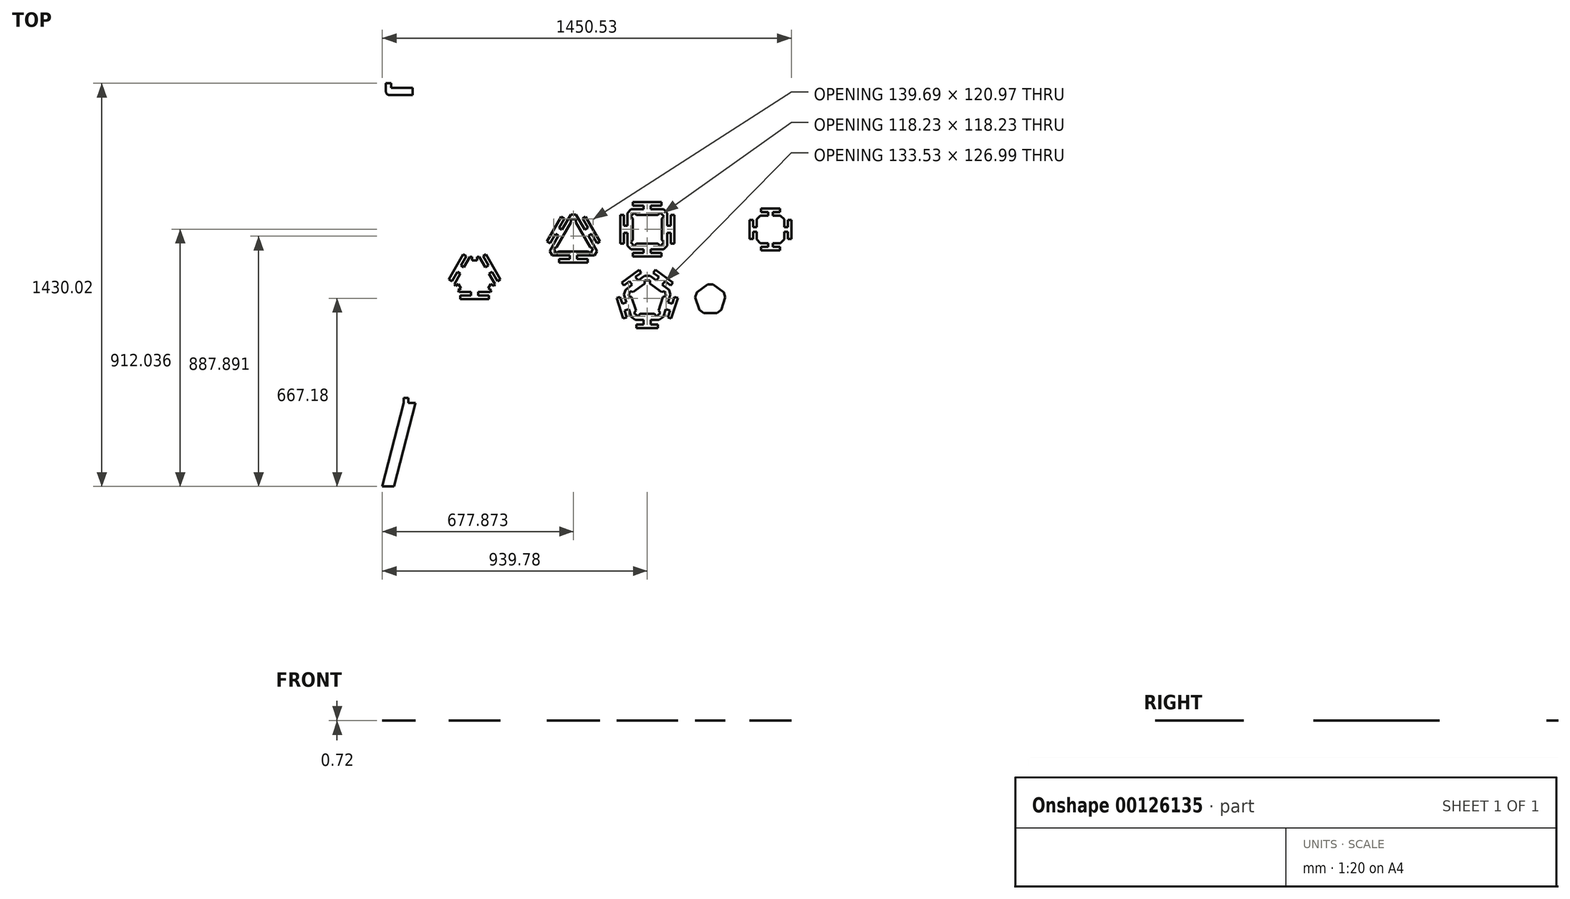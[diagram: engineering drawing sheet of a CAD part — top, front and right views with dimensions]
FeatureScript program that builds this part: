
annotation { "Feature Type Name" : "Feature", "Feature Type Description" : "" }
export const myFeature = defineFeature(function(context is Context, id is Id, definition is map)
    precondition{}
    {
        {
            assignVariable(context, id + "F0", {"name" : "ply34", "anyValue" : 0.72});
        }
        {
            var Q0;
            Q0=qCreatedBy(makeId("Top.planeOp"),FACE);
            var sketch = newSketch(context, id + "F1", { "sketchPlane" : qUnion([Q0])});
            skLineSegment(sketch, "E0.bottom", {"start": v(0, 0) * mm, "end": v(31.75, 0) * mm});
            skLineSegment(sketch, "E0.top", {"start": v(0, 711.2) * mm, "end": v(31.75, 711.2) * mm});
            skLineSegment(sketch, "E0.left", {"start": v(0, 0) * mm, "end": v(0, 711.2) * mm});
            skLineSegment(sketch, "E0.right", {"start": v(31.75, 0) * mm, "end": v(31.75, 711.2) * mm});
            skLineSegment(sketch, "E1.bottom", {"start": v(0, 0) * mm, "end": v(41.9, 0) * mm});
            skLineSegment(sketch, "E1.top", {"start": v(0, -406.4) * mm, "end": v(41.91, -406.4) * mm});
            skLineSegment(sketch, "E1.left", {"start": v(0, 0) * mm, "end": v(0, -406.4) * mm});
            skLineSegment(sketch, "E1.right", {"start": v(41.9, 0) * mm, "end": v(41.91, -406.4) * mm});
            skLineSegment(sketch, "E2.bottom", {"start": v(31.75, 711.2) * mm, "end": v(-44.45, 711.2) * mm});
            skLineSegment(sketch, "E2.top", {"start": v(31.75, 685.8) * mm, "end": v(-44.45, 685.8) * mm});
            skLineSegment(sketch, "E2.left", {"start": v(31.75, 711.2) * mm, "end": v(31.75, 685.8) * mm});
            skLineSegment(sketch, "E2.right", {"start": v(-44.45, 711.2) * mm, "end": v(-44.45, 685.8) * mm});
            skLineSegment(sketch, "E3.bottom", {"start": v(-44.45, 685.8) * mm, "end": v(-50.8, 685.8) * mm});
            skLineSegment(sketch, "E3.top", {"start": v(-44.45, 727.7) * mm, "end": v(-63.5, 727.7) * mm});
            skLineSegment(sketch, "E3.left", {"start": v(-44.45, 685.8) * mm, "end": v(-44.45, 727.7) * mm});
            skLineSegment(sketch, "E3.right", {"start": v(-63.5, 698.5) * mm, "end": v(-63.5, 727.7) * mm});
            skLineSegment(sketch, "E4.bottom", {"start": v(31.75, 711.2) * mm, "end": v(12.7, 711.2) * mm});
            skLineSegment(sketch, "E4.top", {"start": v(31.75, 727.7) * mm, "end": v(12.7, 727.7) * mm});
            skLineSegment(sketch, "E4.left", {"start": v(31.75, 711.2) * mm, "end": v(31.75, 727.7) * mm});
            skLineSegment(sketch, "E4.right", {"start": v(12.7, 711.2) * mm, "end": v(12.7, 727.7) * mm});
            skLineSegment(sketch, "E5.bottom", {"start": v(0, -406.4) * mm, "end": v(16.51, -406.4) * mm});
            skLineSegment(sketch, "E5.top", {"start": v(0, -388.11) * mm, "end": v(16.51, -388.11) * mm});
            skLineSegment(sketch, "E5.left", {"start": v(0, -406.4) * mm, "end": v(0, -388.11) * mm});
            skLineSegment(sketch, "E5.right", {"start": v(16.51, -406.4) * mm, "end": v(16.51, -388.11) * mm});
            skLineSegment(sketch, "E6.bottom", {"start": v(0, 431.8) * mm, "end": v(16.51, 431.8) * mm});
            skLineSegment(sketch, "E6.top", {"start": v(0, 413.51) * mm, "end": v(16.51, 413.51) * mm});
            skLineSegment(sketch, "E6.left", {"start": v(0, 431.8) * mm, "end": v(0, 413.51) * mm});
            skLineSegment(sketch, "E6.right", {"start": v(16.51, 431.8) * mm, "end": v(16.51, 413.51) * mm});
            skLineSegment(sketch, "E7.0", {"start": v(194.06, 15.84) * mm, "end": v(242.06, 98.99) * mm});
            skLineSegment(sketch, "E7.1", {"start": v(260.35, 98.99) * mm, "end": v(308.36, 15.84) * mm});
            skLineSegment(sketch, "E7.2", {"start": v(299.21, 0) * mm, "end": v(203.2, 0) * mm});
            skLineSegment(sketch, "E8", {"start": v(242.06, 98.99) * mm, "end": v(260.35, 98.99) * mm});
            skLineSegment(sketch, "E9", {"start": v(308.36, 15.84) * mm, "end": v(299.21, 0) * mm});
            skLineSegment(sketch, "E10", {"start": v(194.06, 15.84) * mm, "end": v(203.2, 0) * mm});
            skLineSegment(sketch, "E11.0", {"start": v(541.73, 146.65) * mm, "end": v(592.53, 234.64) * mm});
            skLineSegment(sketch, "E11.1", {"start": v(610.82, 234.64) * mm, "end": v(661.62, 146.65) * mm});
            skLineSegment(sketch, "E11.2", {"start": v(652.47, 130.81) * mm, "end": v(550.87, 130.81) * mm});
            skLineSegment(sketch, "E12", {"start": v(592.53, 234.64) * mm, "end": v(610.82, 234.64) * mm});
            skLineSegment(sketch, "E13", {"start": v(661.62, 146.65) * mm, "end": v(652.47, 130.81) * mm});
            skLineSegment(sketch, "E14", {"start": v(541.73, 146.65) * mm, "end": v(550.87, 130.81) * mm});
            skLineSegment(sketch, "E15.0", {"start": v(517.53, 132.68) * mm, "end": v(592.53, 262.58) * mm});
            skLineSegment(sketch, "E15.1", {"start": v(610.82, 262.58) * mm, "end": v(685.81, 132.68) * mm});
            skLineSegment(sketch, "E15.2", {"start": v(685.81, 132.68) * mm, "end": v(676.67, 116.84) * mm});
            skLineSegment(sketch, "E15.3", {"start": v(592.53, 262.58) * mm, "end": v(610.82, 262.58) * mm});
            skLineSegment(sketch, "E15.4", {"start": v(676.67, 116.84) * mm, "end": v(526.68, 116.84) * mm});
            skLineSegment(sketch, "E15.5", {"start": v(517.53, 132.68) * mm, "end": v(526.68, 116.84) * mm});
            skPoint(sketch, "E16", {"position": v(657.04, 138.73) * mm});
            skPoint(sketch, "E17", {"position": v(546.3, 138.73) * mm});
            skLineSegment(sketch, "E18", {"start": v(601.67, 234.64) * mm, "end": v(601.67, 130.81) * mm, "construction": true});
            skLineSegment(sketch, "E19", {"start": v(657.04, 138.73) * mm, "end": v(506.57, 225.6) * mm, "construction": true});
            skLineSegment(sketch, "E20", {"start": v(546.3, 138.73) * mm, "end": v(636.22, 190.64) * mm, "construction": true});
            skPoint(sketch, "E21", {"position": v(601.67, 272.41) * mm});
            skLineSegment(sketch, "E22.top", {"start": v(592.53, 246.07) * mm, "end": v(610.82, 246.07) * mm});
            skLineSegment(sketch, "E22.left", {"start": v(592.53, 234.64) * mm, "end": v(592.53, 246.07) * mm});
            skLineSegment(sketch, "E22.right", {"start": v(610.82, 234.64) * mm, "end": v(610.82, 246.07) * mm});
            skPoint(sketch, "E23", {"position": v(601.67, 170.7) * mm});
            skLineSegment(sketch, "E24.1.0", {"start": v(540.97, 125.1) * mm, "end": v(531.83, 140.93) * mm});
            skLineSegment(sketch, "E24.1.1", {"start": v(550.87, 130.8) * mm, "end": v(540.97, 125.1) * mm});
            skLineSegment(sketch, "E24.1.2", {"start": v(541.73, 146.65) * mm, "end": v(531.83, 140.93) * mm});
            skLineSegment(sketch, "E24.2.0", {"start": v(671.52, 140.93) * mm, "end": v(662.37, 125.1) * mm});
            skLineSegment(sketch, "E24.2.1", {"start": v(661.62, 146.65) * mm, "end": v(671.52, 140.93) * mm});
            skLineSegment(sketch, "E24.2.2", {"start": v(652.47, 130.81) * mm, "end": v(662.37, 125.1) * mm});
            skLineSegment(sketch, "E25.0", {"start": v(-364.74, -24.05) * mm, "end": v(-313.94, 63.94) * mm, "construction": true});
            skLineSegment(sketch, "E25.1", {"start": v(-295.66, 63.94) * mm, "end": v(-244.86, -24.05) * mm, "construction": true});
            skLineSegment(sketch, "E25.2", {"start": v(-254, -39.89) * mm, "end": v(-355.6, -39.89) * mm, "construction": true});
            skLineSegment(sketch, "E26", {"start": v(-313.94, 63.94) * mm, "end": v(-295.66, 63.94) * mm, "construction": true});
            skLineSegment(sketch, "E27.0", {"start": v(-398.47, -24.05) * mm, "end": v(-330.8, 93.15) * mm, "construction": true});
            skLineSegment(sketch, "E27.1", {"start": v(-278.8, 93.15) * mm, "end": v(-211.13, -24.05) * mm, "construction": true});
            skLineSegment(sketch, "E27.2", {"start": v(-211.13, -24.05) * mm, "end": v(-237.14, -69.1) * mm, "construction": true});
            skLineSegment(sketch, "E27.3", {"start": v(-330.8, 93.15) * mm, "end": v(-278.8, 93.15) * mm, "construction": true});
            skLineSegment(sketch, "E27.4", {"start": v(-237.14, -69.1) * mm, "end": v(-372.46, -69.1) * mm, "construction": true});
            skLineSegment(sketch, "E28", {"start": v(-304.8, 63.94) * mm, "end": v(-304.8, -39.89) * mm, "construction": true});
            skLineSegment(sketch, "E29", {"start": v(-360.17, -31.97) * mm, "end": v(-270.26, 19.94) * mm, "construction": true});
            skPoint(sketch, "E30", {"position": v(-304.8, 109) * mm});
            skLineSegment(sketch, "E31.top", {"start": v(-313.94, 76.64) * mm, "end": v(-295.66, 76.64) * mm, "construction": true});
            skLineSegment(sketch, "E31.left", {"start": v(-313.94, 63.94) * mm, "end": v(-313.94, 76.64) * mm, "construction": true});
            skLineSegment(sketch, "E31.right", {"start": v(-295.66, 63.94) * mm, "end": v(-295.66, 76.64) * mm, "construction": true});
            skLineSegment(sketch, "E32.bottom", {"start": v(-313.94, 89.34) * mm, "end": v(-295.66, 89.34) * mm});
            skLineSegment(sketch, "E32.top", {"start": v(-313.94, 51.24) * mm, "end": v(-295.66, 51.24) * mm});
            skLineSegment(sketch, "E32.left", {"start": v(-313.94, 89.34) * mm, "end": v(-313.94, 51.24) * mm});
            skLineSegment(sketch, "E32.right", {"start": v(-295.66, 89.34) * mm, "end": v(-295.66, 51.24) * mm});
            skLineSegment(sketch, "E33.top", {"start": v(-313.94, 38.54) * mm, "end": v(-295.66, 38.54) * mm});
            skLineSegment(sketch, "E33.left", {"start": v(-313.94, 89.34) * mm, "end": v(-313.94, 38.54) * mm});
            skLineSegment(sketch, "E33.right", {"start": v(-295.66, 89.34) * mm, "end": v(-295.66, 38.54) * mm});
            skLineSegment(sketch, "E34.bottom", {"start": v(-295.66, 89.34) * mm, "end": v(-313.94, 89.34) * mm});
            skLineSegment(sketch, "E34.top", {"start": v(-295.66, 76.64) * mm, "end": v(-313.94, 76.64) * mm});
            skLineSegment(sketch, "E34.left", {"start": v(-295.66, 89.34) * mm, "end": v(-295.66, 76.64) * mm});
            skLineSegment(sketch, "E34.right", {"start": v(-313.94, 89.34) * mm, "end": v(-313.94, 76.64) * mm});
            skLineSegment(sketch, "E35.0", {"start": v(179.4, 15.84) * mm, "end": v(195.87, -12.7) * mm});
            skLineSegment(sketch, "E35.1", {"start": v(234.73, 111.69) * mm, "end": v(267.68, 111.69) * mm});
            skLineSegment(sketch, "E35.2", {"start": v(267.68, 111.69) * mm, "end": v(323.02, 15.84) * mm});
            skLineSegment(sketch, "E35.3", {"start": v(179.4, 15.84) * mm, "end": v(234.73, 111.69) * mm});
            skLineSegment(sketch, "E35.4", {"start": v(323.02, 15.84) * mm, "end": v(306.54, -12.7) * mm});
            skLineSegment(sketch, "E35.5", {"start": v(306.54, -12.7) * mm, "end": v(195.87, -12.7) * mm});
            skLineSegment(sketch, "E36", {"start": v(242.06, 98.99) * mm, "end": v(242.06, 111.69) * mm});
            skLineSegment(sketch, "E37", {"start": v(260.35, 98.99) * mm, "end": v(260.35, 111.69) * mm});
            skLineSegment(sketch, "E38", {"start": v(251.2, 98.99) * mm, "end": v(251.2, 0) * mm, "construction": true});
            skLineSegment(sketch, "E39", {"start": v(303.78, 7.92) * mm, "end": v(218.06, 57.41) * mm, "construction": true});
            skPoint(sketch, "E39.endSnap0", {"position": v(218.06, 57.41) * mm});
            skPoint(sketch, "E40", {"position": v(251.2, 38.27) * mm});
            skLineSegment(sketch, "E41.1.0", {"start": v(194.06, 15.84) * mm, "end": v(183.06, 9.49) * mm});
            skLineSegment(sketch, "E41.1.1", {"start": v(203.2, 0) * mm, "end": v(192.2, -6.35) * mm});
            skLineSegment(sketch, "E41.1.2", {"start": v(203.2, 0) * mm, "end": v(194.06, 15.84) * mm});
            skLineSegment(sketch, "E41.2.0", {"start": v(299.21, 0) * mm, "end": v(310.21, -6.35) * mm});
            skLineSegment(sketch, "E41.2.1", {"start": v(308.36, 15.84) * mm, "end": v(319.35, 9.49) * mm});
            skLineSegment(sketch, "E42", {"start": v(-364.74, -24.05) * mm, "end": v(-355.6, -39.89) * mm, "construction": true});
            skLineSegment(sketch, "E43", {"start": v(-254, -39.89) * mm, "end": v(-244.86, -24.05) * mm, "construction": true});
            skLineSegment(sketch, "E44", {"start": v(-398.47, -24.05) * mm, "end": v(-372.46, -69.1) * mm, "construction": true});
            skPoint(sketch, "E45", {"position": v(-304.8, 0) * mm});
            skLineSegment(sketch, "E46.1.0", {"start": v(-333.6, -27.19) * mm, "end": v(-342.75, -11.35) * mm});
            skLineSegment(sketch, "E46.1.1", {"start": v(-355.6, -39.89) * mm, "end": v(-364.74, -24.05) * mm, "construction": true});
            skLineSegment(sketch, "E46.1.2", {"start": v(-377.6, -52.59) * mm, "end": v(-386.74, -36.75) * mm});
            skLineSegment(sketch, "E46.1.3", {"start": v(-377.6, -52.59) * mm, "end": v(-366.6, -46.24) * mm});
            skLineSegment(sketch, "E46.1.4", {"start": v(-386.74, -36.75) * mm, "end": v(-353.75, -17.7) * mm});
            skLineSegment(sketch, "E46.1.5", {"start": v(-344.6, -33.54) * mm, "end": v(-353.75, -17.7) * mm});
            skLineSegment(sketch, "E46.1.6", {"start": v(-366.6, -46.24) * mm, "end": v(-375.74, -30.4) * mm, "construction": true});
            skLineSegment(sketch, "E46.1.7", {"start": v(-377.6, -52.59) * mm, "end": v(-344.6, -33.54) * mm});
            skLineSegment(sketch, "E46.1.8", {"start": v(-377.6, -52.59) * mm, "end": v(-333.6, -27.19) * mm});
            skLineSegment(sketch, "E46.1.9", {"start": v(-364.74, -24.05) * mm, "end": v(-375.74, -30.4) * mm, "construction": true});
            skLineSegment(sketch, "E46.1.10", {"start": v(-386.74, -36.75) * mm, "end": v(-342.75, -11.35) * mm});
            skLineSegment(sketch, "E46.1.11", {"start": v(-355.6, -39.89) * mm, "end": v(-366.6, -46.24) * mm, "construction": true});
            skPoint(sketch, "E46.1.12", {"position": v(-399.2, -54.5) * mm});
            skLineSegment(sketch, "E46.1.13", {"start": v(-375.74, -30.4) * mm, "end": v(-366.6, -46.24) * mm});
            skLineSegment(sketch, "E46.1.14", {"start": v(-386.74, -36.75) * mm, "end": v(-375.74, -30.4) * mm});
            skLineSegment(sketch, "E46.1.15", {"start": v(-386.74, -36.75) * mm, "end": v(-377.6, -52.59) * mm});
            skLineSegment(sketch, "E46.1.16", {"start": v(-355.6, -39.89) * mm, "end": v(-364.74, -24.05) * mm, "construction": true});
            skLineSegment(sketch, "E46.1.17", {"start": v(-377.6, -52.59) * mm, "end": v(-386.74, -36.75) * mm});
            skLineSegment(sketch, "E46.2.0", {"start": v(-266.85, -11.35) * mm, "end": v(-276, -27.19) * mm});
            skLineSegment(sketch, "E46.2.1", {"start": v(-244.86, -24.05) * mm, "end": v(-254, -39.89) * mm, "construction": true});
            skLineSegment(sketch, "E46.2.2", {"start": v(-222.86, -36.75) * mm, "end": v(-232, -52.59) * mm});
            skLineSegment(sketch, "E46.2.3", {"start": v(-222.86, -36.75) * mm, "end": v(-233.86, -30.4) * mm});
            skLineSegment(sketch, "E46.2.4", {"start": v(-232, -52.59) * mm, "end": v(-265, -33.54) * mm});
            skLineSegment(sketch, "E46.2.5", {"start": v(-255.85, -17.7) * mm, "end": v(-265, -33.54) * mm});
            skLineSegment(sketch, "E46.2.6", {"start": v(-233.86, -30.4) * mm, "end": v(-243, -46.24) * mm, "construction": true});
            skLineSegment(sketch, "E46.2.7", {"start": v(-222.86, -36.75) * mm, "end": v(-255.85, -17.7) * mm});
            skLineSegment(sketch, "E46.2.8", {"start": v(-222.86, -36.75) * mm, "end": v(-266.85, -11.35) * mm});
            skLineSegment(sketch, "E46.2.9", {"start": v(-254, -39.89) * mm, "end": v(-243, -46.24) * mm, "construction": true});
            skLineSegment(sketch, "E46.2.10", {"start": v(-232, -52.59) * mm, "end": v(-276, -27.19) * mm});
            skLineSegment(sketch, "E46.2.11", {"start": v(-244.86, -24.05) * mm, "end": v(-233.86, -30.4) * mm, "construction": true});
            skPoint(sketch, "E46.2.12", {"position": v(-210.4, -54.5) * mm});
            skLineSegment(sketch, "E46.2.13", {"start": v(-243, -46.24) * mm, "end": v(-233.86, -30.4) * mm});
            skLineSegment(sketch, "E46.2.14", {"start": v(-232, -52.59) * mm, "end": v(-243, -46.24) * mm});
            skLineSegment(sketch, "E46.2.15", {"start": v(-232, -52.59) * mm, "end": v(-222.86, -36.75) * mm});
            skLineSegment(sketch, "E46.2.16", {"start": v(-244.86, -24.05) * mm, "end": v(-254, -39.89) * mm, "construction": true});
            skLineSegment(sketch, "E46.2.17", {"start": v(-222.86, -36.75) * mm, "end": v(-232, -52.59) * mm});
            skPoint(sketch, "E47", {"position": v(601.67, 116.84) * mm});
            skPoint(sketch, "E48", {"position": v(601.67, 262.58) * mm});
            skPoint(sketch, "E49", {"position": v(601.67, 246.07) * mm});
            skLineSegment(sketch, "E50", {"start": v(41.91, -406.4) * mm, "end": v(41.91, -702.31) * mm, "construction": true});
            skLineSegment(sketch, "E51", {"start": v(0, -406.4) * mm, "end": v(0, -702.31) * mm, "construction": true});
            skLineSegment(sketch, "E52", {"start": v(41.91, -457.2) * mm, "end": v(0, -457.2) * mm, "construction": true});
            skArc(sketch, "E53", {"start": v(-34.29, -702.31) * mm, "mid": v(26.28, -560.14) * mm, "end": v(41.91, -406.4) * mm, "construction": true});
            skArc(sketch, "E54", {"start": v(-76.2, -702.31) * mm, "mid": v(-15.63, -560.14) * mm, "end": v(0, -406.4) * mm, "construction": true});
            skLineSegment(sketch, "E55", {"start": v(-76.2, -702.31) * mm, "end": v(-34.29, -702.31) * mm});
            skPoint(sketch, "E56.visualSharp", {"position": v(-63.5, 685.8) * mm});
            skArc(sketch, "E56.filletArc", {"start": v(-63.5, 698.5) * mm, "mid": v(-59.78, 689.52) * mm, "end": v(-50.8, 685.8) * mm});
            skLineSegment(sketch, "E57.0", {"start": v(191.26, 297.58) * mm, "end": v(242.06, 385.57) * mm, "construction": true});
            skLineSegment(sketch, "E57.1", {"start": v(260.35, 385.57) * mm, "end": v(311.15, 297.58) * mm, "construction": true});
            skLineSegment(sketch, "E57.2", {"start": v(302, 281.75) * mm, "end": v(200.4, 281.75) * mm, "construction": true});
            skLineSegment(sketch, "E58", {"start": v(242.06, 385.57) * mm, "end": v(260.35, 385.57) * mm, "construction": true});
            skLineSegment(sketch, "E59", {"start": v(311.15, 297.58) * mm, "end": v(302, 281.75) * mm, "construction": true});
            skLineSegment(sketch, "E60", {"start": v(191.26, 297.58) * mm, "end": v(200.4, 281.75) * mm, "construction": true});
            skLineSegment(sketch, "E61.0", {"start": v(167.07, 283.61) * mm, "end": v(242.06, 413.51) * mm, "construction": true});
            skLineSegment(sketch, "E61.1", {"start": v(260.35, 413.51) * mm, "end": v(335.35, 283.61) * mm, "construction": true});
            skLineSegment(sketch, "E61.2", {"start": v(335.35, 283.61) * mm, "end": v(326.2, 267.78) * mm, "construction": true});
            skLineSegment(sketch, "E61.3", {"start": v(242.06, 413.51) * mm, "end": v(260.35, 413.51) * mm, "construction": true});
            skLineSegment(sketch, "E61.4", {"start": v(326.2, 267.78) * mm, "end": v(176.2, 267.78) * mm, "construction": true});
            skLineSegment(sketch, "E61.5", {"start": v(167.07, 283.61) * mm, "end": v(176.2, 267.78) * mm, "construction": true});
            skPoint(sketch, "E62", {"position": v(306.58, 289.66) * mm});
            skPoint(sketch, "E63", {"position": v(195.83, 289.66) * mm});
            skLineSegment(sketch, "E64", {"start": v(251.2, 385.57) * mm, "end": v(251.2, 281.75) * mm, "construction": true});
            skLineSegment(sketch, "E65", {"start": v(306.58, 289.66) * mm, "end": v(162.6, 372.8) * mm, "construction": true});
            skLineSegment(sketch, "E66", {"start": v(195.83, 289.66) * mm, "end": v(285.75, 341.58) * mm, "construction": true});
            skPoint(sketch, "E67", {"position": v(251.2, 431.16) * mm});
            skLineSegment(sketch, "E68.top", {"start": v(242.06, 397) * mm, "end": v(260.35, 397) * mm, "construction": true});
            skLineSegment(sketch, "E68.left", {"start": v(242.06, 385.57) * mm, "end": v(242.06, 397) * mm, "construction": true});
            skLineSegment(sketch, "E68.right", {"start": v(260.35, 385.57) * mm, "end": v(260.35, 397) * mm, "construction": true});
            skPoint(sketch, "E69", {"position": v(251.2, 321.63) * mm});
            skLineSegment(sketch, "E70.1.0", {"start": v(190.5, 276.03) * mm, "end": v(181.36, 291.87) * mm, "construction": true});
            skLineSegment(sketch, "E70.1.1", {"start": v(200.4, 281.75) * mm, "end": v(190.5, 276.03) * mm, "construction": true});
            skLineSegment(sketch, "E70.1.2", {"start": v(191.26, 297.58) * mm, "end": v(181.36, 291.87) * mm, "construction": true});
            skLineSegment(sketch, "E70.2.0", {"start": v(321.05, 291.87) * mm, "end": v(311.9, 276.03) * mm, "construction": true});
            skLineSegment(sketch, "E70.2.1", {"start": v(311.15, 297.58) * mm, "end": v(321.05, 291.87) * mm, "construction": true});
            skLineSegment(sketch, "E70.2.2", {"start": v(302, 281.75) * mm, "end": v(311.9, 276.03) * mm, "construction": true});
            skPoint(sketch, "E71", {"position": v(251.2, 267.78) * mm});
            skPoint(sketch, "E72", {"position": v(251.2, 413.51) * mm});
            skPoint(sketch, "E73", {"position": v(251.2, 397) * mm});
            skPoint(sketch, "E74", {"position": v(251.2, 111.69) * mm});
            skLineSegment(sketch, "E75.0", {"start": v(242.06, 381.76) * mm, "end": v(260.35, 381.76) * mm});
            skLineSegment(sketch, "E76.0", {"start": v(307.85, 299.49) * mm, "end": v(298.7, 283.65) * mm});
            skLineSegment(sketch, "E77.0", {"start": v(203.7, 283.65) * mm, "end": v(194.56, 299.49) * mm});
            skLineSegment(sketch, "E78", {"start": v(648.32, 197.63) * mm, "end": v(670.31, 210.33) * mm, "construction": true});
            skLineSegment(sketch, "E79", {"start": v(670.31, 210.33) * mm, "end": v(663.96, 221.33) * mm});
            skLineSegment(sketch, "E80", {"start": v(663.96, 221.33) * mm, "end": v(641.97, 208.63) * mm});
            skLineSegment(sketch, "E81.MirrorCS", {"start": v(670.31, 210.33) * mm, "end": v(676.66, 199.33) * mm});
            skLineSegment(sketch, "E82.MirrorCS", {"start": v(676.66, 199.33) * mm, "end": v(654.67, 186.63) * mm});
            skLineSegment(sketch, "E83", {"start": v(663.96, 221.33) * mm, "end": v(644.91, 254.32) * mm});
            skLineSegment(sketch, "E84.MirrorCS", {"start": v(676.66, 199.33) * mm, "end": v(695.71, 166.33) * mm});
            skLineSegment(sketch, "E85", {"start": v(644.91, 254.32) * mm, "end": v(633.91, 247.97) * mm});
            skLineSegment(sketch, "E86", {"start": v(633.91, 247.97) * mm, "end": v(652.96, 214.98) * mm});
            skLineSegment(sketch, "E87.MirrorCS", {"start": v(684.71, 159.98) * mm, "end": v(665.66, 192.98) * mm});
            skLineSegment(sketch, "E88.MirrorCS", {"start": v(695.71, 166.33) * mm, "end": v(684.71, 159.98) * mm});
            skLineSegment(sketch, "E89.1.0", {"start": v(518.63, 159.98) * mm, "end": v(537.68, 192.98) * mm});
            skLineSegment(sketch, "E89.1.1", {"start": v(507.63, 166.33) * mm, "end": v(518.63, 159.98) * mm});
            skLineSegment(sketch, "E89.1.2", {"start": v(526.68, 199.33) * mm, "end": v(507.63, 166.33) * mm});
            skLineSegment(sketch, "E89.1.3", {"start": v(533.03, 210.33) * mm, "end": v(526.68, 199.33) * mm});
            skLineSegment(sketch, "E89.1.4", {"start": v(533.03, 210.33) * mm, "end": v(539.38, 221.33) * mm});
            skLineSegment(sketch, "E89.1.5", {"start": v(526.68, 199.33) * mm, "end": v(548.68, 186.63) * mm});
            skLineSegment(sketch, "E89.1.6", {"start": v(539.38, 221.33) * mm, "end": v(561.38, 208.63) * mm});
            skLineSegment(sketch, "E89.1.7", {"start": v(569.43, 247.97) * mm, "end": v(550.38, 214.98) * mm});
            skLineSegment(sketch, "E89.1.8", {"start": v(539.38, 221.33) * mm, "end": v(558.43, 254.32) * mm});
            skLineSegment(sketch, "E89.1.9", {"start": v(558.43, 254.32) * mm, "end": v(569.43, 247.97) * mm});
            skLineSegment(sketch, "E89.2.0", {"start": v(652.47, 104.14) * mm, "end": v(614.37, 104.14) * mm});
            skLineSegment(sketch, "E89.2.1", {"start": v(652.47, 91.44) * mm, "end": v(652.47, 104.14) * mm});
            skLineSegment(sketch, "E89.2.2", {"start": v(614.37, 91.44) * mm, "end": v(652.47, 91.44) * mm});
            skLineSegment(sketch, "E89.2.3", {"start": v(601.67, 91.44) * mm, "end": v(614.37, 91.44) * mm});
            skLineSegment(sketch, "E89.2.4", {"start": v(601.67, 91.44) * mm, "end": v(588.97, 91.44) * mm});
            skLineSegment(sketch, "E89.2.5", {"start": v(614.37, 91.44) * mm, "end": v(614.37, 116.84) * mm});
            skLineSegment(sketch, "E89.2.6", {"start": v(588.97, 91.44) * mm, "end": v(588.97, 116.84) * mm});
            skLineSegment(sketch, "E89.2.7", {"start": v(550.87, 104.14) * mm, "end": v(588.97, 104.14) * mm});
            skLineSegment(sketch, "E89.2.8", {"start": v(588.97, 91.44) * mm, "end": v(550.87, 91.44) * mm});
            skLineSegment(sketch, "E89.2.9", {"start": v(550.87, 91.44) * mm, "end": v(550.87, 104.14) * mm});
            skLineSegment(sketch, "E90", {"start": v(295.35, 63.76) * mm, "end": v(317.35, 76.46) * mm, "construction": true});
            skLineSegment(sketch, "E91", {"start": v(317.35, 76.46) * mm, "end": v(291.95, 120.46) * mm});
            skLineSegment(sketch, "E92", {"start": v(291.95, 120.46) * mm, "end": v(280.95, 114.1) * mm});
            skLineSegment(sketch, "E93", {"start": v(280.95, 114.1) * mm, "end": v(300, 81.11) * mm});
            skLineSegment(sketch, "E94", {"start": v(300, 81.11) * mm, "end": v(289, 74.76) * mm});
            skLineSegment(sketch, "E95.MirrorCS", {"start": v(317.35, 76.46) * mm, "end": v(342.75, 32.47) * mm});
            skLineSegment(sketch, "E96.MirrorCS", {"start": v(342.75, 32.47) * mm, "end": v(331.75, 26.12) * mm});
            skLineSegment(sketch, "E97.MirrorCS", {"start": v(331.75, 26.12) * mm, "end": v(312.7, 59.11) * mm});
            skLineSegment(sketch, "E98.MirrorCS", {"start": v(312.7, 59.11) * mm, "end": v(301.7, 52.76) * mm});
            skLineSegment(sketch, "E99.1.0", {"start": v(189.71, 59.11) * mm, "end": v(200.71, 52.76) * mm});
            skLineSegment(sketch, "E99.1.1", {"start": v(202.41, 81.11) * mm, "end": v(213.41, 74.76) * mm});
            skLineSegment(sketch, "E99.1.2", {"start": v(170.66, 26.12) * mm, "end": v(189.71, 59.11) * mm});
            skLineSegment(sketch, "E99.1.3", {"start": v(185.06, 76.46) * mm, "end": v(159.66, 32.47) * mm});
            skLineSegment(sketch, "E99.1.4", {"start": v(207.06, 63.76) * mm, "end": v(185.06, 76.46) * mm, "construction": true});
            skLineSegment(sketch, "E99.1.5", {"start": v(159.66, 32.47) * mm, "end": v(170.66, 26.12) * mm});
            skLineSegment(sketch, "E99.1.6", {"start": v(185.06, 76.46) * mm, "end": v(210.46, 120.46) * mm});
            skLineSegment(sketch, "E99.1.7", {"start": v(210.46, 120.46) * mm, "end": v(221.46, 114.1) * mm});
            skLineSegment(sketch, "E99.1.8", {"start": v(221.46, 114.1) * mm, "end": v(202.41, 81.11) * mm});
            skLineSegment(sketch, "E99.2.0", {"start": v(263.9, -25.4) * mm, "end": v(263.9, -12.7) * mm});
            skLineSegment(sketch, "E99.2.1", {"start": v(238.5, -25.4) * mm, "end": v(238.5, -12.7) * mm});
            skLineSegment(sketch, "E99.2.2", {"start": v(302, -25.4) * mm, "end": v(263.9, -25.4) * mm});
            skLineSegment(sketch, "E99.2.3", {"start": v(251.2, -38.1) * mm, "end": v(302, -38.1) * mm});
            skLineSegment(sketch, "E99.2.4", {"start": v(251.2, -12.7) * mm, "end": v(251.2, -38.1) * mm, "construction": true});
            skLineSegment(sketch, "E99.2.5", {"start": v(302, -38.1) * mm, "end": v(302, -25.4) * mm});
            skLineSegment(sketch, "E99.2.6", {"start": v(251.2, -38.1) * mm, "end": v(200.4, -38.1) * mm});
            skLineSegment(sketch, "E99.2.7", {"start": v(200.4, -38.1) * mm, "end": v(200.4, -25.4) * mm});
            skLineSegment(sketch, "E99.2.8", {"start": v(200.4, -25.4) * mm, "end": v(238.5, -25.4) * mm});
            skLineSegment(sketch, "E100", {"start": v(0, -406.4) * mm, "end": v(-76.2, -702.31) * mm});
            skLineSegment(sketch, "E101", {"start": v(-34.29, -702.31) * mm, "end": v(41.91, -406.4) * mm});
            skLineSegment(sketch, "E102.bottom", {"start": v(792.8, 280.51) * mm, "end": v(934.37, 280.51) * mm});
            skLineSegment(sketch, "E102.top", {"start": v(792.8, 138.94) * mm, "end": v(934.37, 138.94) * mm});
            skLineSegment(sketch, "E102.left", {"start": v(792.8, 280.51) * mm, "end": v(792.8, 138.94) * mm});
            skLineSegment(sketch, "E102.right", {"start": v(934.37, 280.51) * mm, "end": v(934.37, 138.94) * mm});
            skLineSegment(sketch, "E103", {"start": v(805.72, 280.51) * mm, "end": v(792.8, 267.58) * mm});
            skLineSegment(sketch, "E104", {"start": v(805.72, 280.51) * mm, "end": v(825.48, 260.76) * mm, "construction": true});
            skLineSegment(sketch, "E105", {"start": v(825.48, 260.76) * mm, "end": v(812.55, 247.83) * mm});
            skLineSegment(sketch, "E106", {"start": v(812.55, 247.83) * mm, "end": v(792.8, 267.58) * mm, "construction": true});
            skLineSegment(sketch, "E107", {"start": v(812.55, 247.83) * mm, "end": v(804.47, 255.9) * mm});
            skLineSegment(sketch, "E108", {"start": v(804.47, 255.9) * mm, "end": v(817.4, 268.84) * mm});
            skLineSegment(sketch, "E109", {"start": v(817.4, 268.84) * mm, "end": v(825.48, 260.76) * mm});
            skPoint(sketch, "E110", {"position": v(863.58, 209.73) * mm});
            skPoint(sketch, "E110.positionSnap0", {"position": v(792.8, 209.73) * mm});
            skPoint(sketch, "E110.positionSnap1", {"position": v(863.58, 280.51) * mm});
            skLineSegment(sketch, "E111.1.0", {"start": v(817.4, 150.61) * mm, "end": v(804.47, 163.54) * mm});
            skLineSegment(sketch, "E111.1.1", {"start": v(804.47, 163.54) * mm, "end": v(812.55, 171.63) * mm});
            skLineSegment(sketch, "E111.1.2", {"start": v(812.55, 171.63) * mm, "end": v(825.48, 158.7) * mm});
            skLineSegment(sketch, "E111.1.3", {"start": v(825.48, 158.7) * mm, "end": v(817.4, 150.61) * mm});
            skLineSegment(sketch, "E111.2.0", {"start": v(922.7, 163.54) * mm, "end": v(909.76, 150.61) * mm});
            skLineSegment(sketch, "E111.2.1", {"start": v(909.76, 150.61) * mm, "end": v(901.68, 158.7) * mm});
            skLineSegment(sketch, "E111.2.2", {"start": v(901.68, 158.7) * mm, "end": v(914.61, 171.63) * mm});
            skLineSegment(sketch, "E111.2.3", {"start": v(914.61, 171.63) * mm, "end": v(922.7, 163.54) * mm});
            skLineSegment(sketch, "E111.3.0", {"start": v(909.76, 268.84) * mm, "end": v(922.7, 255.9) * mm});
            skLineSegment(sketch, "E111.3.1", {"start": v(922.7, 255.9) * mm, "end": v(914.61, 247.83) * mm});
            skLineSegment(sketch, "E111.3.2", {"start": v(914.61, 247.83) * mm, "end": v(901.68, 260.76) * mm});
            skLineSegment(sketch, "E111.3.3", {"start": v(901.68, 260.76) * mm, "end": v(909.76, 268.84) * mm});
            skLineSegment(sketch, "E112", {"start": v(825.48, 260.76) * mm, "end": v(901.68, 260.76) * mm});
            skLineSegment(sketch, "E113", {"start": v(914.61, 247.83) * mm, "end": v(914.61, 171.63) * mm});
            skLineSegment(sketch, "E114", {"start": v(812.55, 247.83) * mm, "end": v(812.55, 171.63) * mm});
            skLineSegment(sketch, "E115", {"start": v(825.48, 158.7) * mm, "end": v(901.68, 158.7) * mm});
            skLineSegment(sketch, "E116.1.0", {"start": v(792.8, 151.87) * mm, "end": v(805.72, 138.94) * mm});
            skLineSegment(sketch, "E116.2.0", {"start": v(921.44, 138.94) * mm, "end": v(934.37, 151.87) * mm});
            skLineSegment(sketch, "E116.3.0", {"start": v(934.37, 267.58) * mm, "end": v(921.44, 280.51) * mm});
            skCircle(sketch, "E117.cCircle", {"center": v(863.58, -38.86) * mm, "radius": 73.12 * mm, "construction": true});
            skLineSegment(sketch, "E117.0", {"start": v(863.58, 51.52) * mm, "end": v(949.54, -10.93) * mm});
            skLineSegment(sketch, "E117.1", {"start": v(949.54, -10.93) * mm, "end": v(916.7, -111.98) * mm});
            skLineSegment(sketch, "E117.2", {"start": v(916.7, -111.98) * mm, "end": v(810.45, -111.98) * mm});
            skLineSegment(sketch, "E117.3", {"start": v(810.45, -111.98) * mm, "end": v(777.62, -10.93) * mm});
            skLineSegment(sketch, "E117.4", {"start": v(777.62, -10.93) * mm, "end": v(863.58, 51.52) * mm});
            skPoint(sketch, "E117.0.midPoint", {"position": v(906.56, 20.3) * mm});
            skPoint(sketch, "E118", {"position": v(863.58, 138.94) * mm});
            skLineSegment(sketch, "E119", {"start": v(854.44, 44.88) * mm, "end": v(872.72, 44.88) * mm});
            skLineSegment(sketch, "E120", {"start": v(854.44, 44.88) * mm, "end": v(854.44, 28.37) * mm, "construction": true});
            skLineSegment(sketch, "E121", {"start": v(854.44, 16.94) * mm, "end": v(872.72, 16.94) * mm});
            skLineSegment(sketch, "E122", {"start": v(872.72, 16.94) * mm, "end": v(872.72, 28.37) * mm});
            skLineSegment(sketch, "E123", {"start": v(854.44, 28.37) * mm, "end": v(872.72, 28.37) * mm});
            skLineSegment(sketch, "E124", {"start": v(854.44, 28.37) * mm, "end": v(854.44, 16.94) * mm});
            skLineSegment(sketch, "E125", {"start": v(872.72, 28.37) * mm, "end": v(872.72, 44.88) * mm, "construction": true});
            skLineSegment(sketch, "E126.1.0", {"start": v(796.82, -26.78) * mm, "end": v(807.69, -30.32) * mm});
            skLineSegment(sketch, "E126.1.1", {"start": v(796.82, -26.78) * mm, "end": v(802.47, -9.4) * mm});
            skLineSegment(sketch, "E126.1.2", {"start": v(813.34, -12.92) * mm, "end": v(802.47, -9.4) * mm});
            skLineSegment(sketch, "E126.1.3", {"start": v(807.69, -30.32) * mm, "end": v(813.34, -12.92) * mm});
            skLineSegment(sketch, "E126.1.4", {"start": v(781.11, -21.68) * mm, "end": v(786.77, -4.29) * mm});
            skLineSegment(sketch, "E126.2.0", {"start": v(831.46, -98.63) * mm, "end": v(838.18, -89.38) * mm});
            skLineSegment(sketch, "E126.2.1", {"start": v(831.46, -98.63) * mm, "end": v(816.67, -87.88) * mm});
            skLineSegment(sketch, "E126.2.2", {"start": v(823.38, -78.63) * mm, "end": v(816.67, -87.88) * mm});
            skLineSegment(sketch, "E126.2.3", {"start": v(838.18, -89.38) * mm, "end": v(823.38, -78.63) * mm});
            skLineSegment(sketch, "E126.2.4", {"start": v(821.76, -111.98) * mm, "end": v(806.96, -101.23) * mm});
            skLineSegment(sketch, "E126.3.0", {"start": v(910.5, -87.88) * mm, "end": v(903.77, -78.63) * mm});
            skLineSegment(sketch, "E126.3.1", {"start": v(910.5, -87.88) * mm, "end": v(895.7, -98.63) * mm});
            skLineSegment(sketch, "E126.3.2", {"start": v(888.98, -89.38) * mm, "end": v(895.7, -98.63) * mm});
            skLineSegment(sketch, "E126.3.3", {"start": v(903.77, -78.63) * mm, "end": v(888.98, -89.38) * mm});
            skLineSegment(sketch, "E126.3.4", {"start": v(920.2, -101.23) * mm, "end": v(905.4, -111.98) * mm});
            skLineSegment(sketch, "E126.4.0", {"start": v(924.7, -9.4) * mm, "end": v(913.82, -12.92) * mm});
            skLineSegment(sketch, "E126.4.1", {"start": v(924.7, -9.4) * mm, "end": v(930.34, -26.78) * mm});
            skLineSegment(sketch, "E126.4.2", {"start": v(919.47, -30.32) * mm, "end": v(930.34, -26.78) * mm});
            skLineSegment(sketch, "E126.4.3", {"start": v(913.82, -12.92) * mm, "end": v(919.47, -30.32) * mm});
            skLineSegment(sketch, "E126.4.4", {"start": v(940.4, -4.29) * mm, "end": v(946.05, -21.68) * mm});
            skLineSegment(sketch, "E127", {"start": v(872.72, 16.94) * mm, "end": v(913.82, -12.92) * mm});
            skLineSegment(sketch, "E128", {"start": v(919.47, -30.32) * mm, "end": v(903.77, -78.63) * mm});
            skLineSegment(sketch, "E129", {"start": v(888.98, -89.38) * mm, "end": v(838.18, -89.38) * mm});
            skLineSegment(sketch, "E130", {"start": v(823.38, -78.63) * mm, "end": v(807.69, -30.32) * mm});
            skLineSegment(sketch, "E131", {"start": v(813.34, -12.92) * mm, "end": v(854.44, 16.94) * mm});
            skLineSegment(sketch, "E132.bottom", {"start": v(1031.14, 280.51) * mm, "end": v(1172.72, 280.51) * mm, "construction": true});
            skLineSegment(sketch, "E132.top", {"start": v(1031.14, 138.94) * mm, "end": v(1172.72, 138.94) * mm, "construction": true});
            skLineSegment(sketch, "E132.left", {"start": v(1031.14, 280.51) * mm, "end": v(1031.14, 138.94) * mm, "construction": true});
            skLineSegment(sketch, "E132.right", {"start": v(1172.72, 280.51) * mm, "end": v(1172.72, 138.94) * mm, "construction": true});
            skLineSegment(sketch, "E133", {"start": v(1044.07, 280.51) * mm, "end": v(1031.14, 267.58) * mm, "construction": true});
            skLineSegment(sketch, "E134", {"start": v(1044.07, 280.51) * mm, "end": v(1063.83, 260.76) * mm, "construction": true});
            skLineSegment(sketch, "E135", {"start": v(1063.83, 260.76) * mm, "end": v(1050.9, 247.83) * mm, "construction": true});
            skLineSegment(sketch, "E136", {"start": v(1050.9, 247.83) * mm, "end": v(1031.14, 267.58) * mm, "construction": true});
            skLineSegment(sketch, "E137", {"start": v(1050.9, 247.83) * mm, "end": v(1042.81, 255.9) * mm, "construction": true});
            skLineSegment(sketch, "E138", {"start": v(1042.81, 255.9) * mm, "end": v(1055.75, 268.84) * mm, "construction": true});
            skLineSegment(sketch, "E139", {"start": v(1055.75, 268.84) * mm, "end": v(1063.83, 260.76) * mm, "construction": true});
            skPoint(sketch, "E140", {"position": v(1101.93, 209.73) * mm});
            skPoint(sketch, "E140.positionSnap0", {"position": v(1031.14, 209.73) * mm});
            skPoint(sketch, "E140.positionSnap1", {"position": v(1101.93, 280.51) * mm});
            skLineSegment(sketch, "E141.1.0", {"start": v(1055.75, 150.61) * mm, "end": v(1042.81, 163.54) * mm, "construction": true});
            skLineSegment(sketch, "E141.1.1", {"start": v(1042.81, 163.54) * mm, "end": v(1050.9, 171.63) * mm, "construction": true});
            skLineSegment(sketch, "E141.1.2", {"start": v(1050.9, 171.63) * mm, "end": v(1063.83, 158.7) * mm, "construction": true});
            skLineSegment(sketch, "E141.1.3", {"start": v(1063.83, 158.7) * mm, "end": v(1055.75, 150.61) * mm, "construction": true});
            skLineSegment(sketch, "E141.2.0", {"start": v(1161.04, 163.54) * mm, "end": v(1148.11, 150.61) * mm, "construction": true});
            skLineSegment(sketch, "E141.2.1", {"start": v(1148.11, 150.61) * mm, "end": v(1140.03, 158.7) * mm, "construction": true});
            skLineSegment(sketch, "E141.2.2", {"start": v(1140.03, 158.7) * mm, "end": v(1152.96, 171.63) * mm, "construction": true});
            skLineSegment(sketch, "E141.2.3", {"start": v(1152.96, 171.63) * mm, "end": v(1161.04, 163.54) * mm, "construction": true});
            skLineSegment(sketch, "E141.3.0", {"start": v(1148.11, 268.84) * mm, "end": v(1161.04, 255.9) * mm, "construction": true});
            skLineSegment(sketch, "E141.3.1", {"start": v(1161.04, 255.9) * mm, "end": v(1152.96, 247.83) * mm, "construction": true});
            skLineSegment(sketch, "E141.3.2", {"start": v(1152.96, 247.83) * mm, "end": v(1140.03, 260.76) * mm, "construction": true});
            skLineSegment(sketch, "E141.3.3", {"start": v(1140.03, 260.76) * mm, "end": v(1148.11, 268.84) * mm, "construction": true});
            skLineSegment(sketch, "E142", {"start": v(1063.83, 260.76) * mm, "end": v(1140.03, 260.76) * mm, "construction": true});
            skLineSegment(sketch, "E143", {"start": v(1152.96, 247.83) * mm, "end": v(1152.96, 171.63) * mm, "construction": true});
            skLineSegment(sketch, "E144", {"start": v(1050.9, 247.83) * mm, "end": v(1050.9, 171.63) * mm, "construction": true});
            skLineSegment(sketch, "E145", {"start": v(1063.83, 158.7) * mm, "end": v(1140.03, 158.7) * mm, "construction": true});
            skLineSegment(sketch, "E146.1.0", {"start": v(1031.14, 151.87) * mm, "end": v(1044.07, 138.94) * mm, "construction": true});
            skLineSegment(sketch, "E146.2.0", {"start": v(1159.78, 138.94) * mm, "end": v(1172.72, 151.87) * mm, "construction": true});
            skLineSegment(sketch, "E146.3.0", {"start": v(1172.72, 267.58) * mm, "end": v(1159.78, 280.51) * mm, "construction": true});
            skPoint(sketch, "E147", {"position": v(1101.93, 138.94) * mm});
            skLineSegment(sketch, "E148.0", {"start": v(1050.9, 242.44) * mm, "end": v(1069.22, 260.76) * mm, "construction": true});
            skLineSegment(sketch, "E149.1.0", {"start": v(1069.22, 158.7) * mm, "end": v(1050.9, 177.01) * mm, "construction": true});
            skLineSegment(sketch, "E149.2.0", {"start": v(1152.96, 177.01) * mm, "end": v(1134.64, 158.7) * mm, "construction": true});
            skLineSegment(sketch, "E149.3.0", {"start": v(1134.64, 260.76) * mm, "end": v(1152.96, 242.44) * mm, "construction": true});
            skLineSegment(sketch, "E150.bottom", {"start": v(1251.24, 258.57) * mm, "end": v(1348.93, 258.57) * mm});
            skLineSegment(sketch, "E150.top", {"start": v(1251.24, 160.88) * mm, "end": v(1348.93, 160.88) * mm});
            skLineSegment(sketch, "E150.left", {"start": v(1251.24, 258.57) * mm, "end": v(1251.24, 160.88) * mm});
            skLineSegment(sketch, "E150.right", {"start": v(1348.93, 258.57) * mm, "end": v(1348.93, 160.88) * mm});
            skPoint(sketch, "E150.middle", {"position": v(1300.09, 209.73) * mm});
            skLineSegment(sketch, "E151", {"start": v(1251.24, 245.64) * mm, "end": v(1264.17, 258.57) * mm});
            skLineSegment(sketch, "E152.1.0", {"start": v(1264.17, 160.88) * mm, "end": v(1251.24, 173.81) * mm});
            skLineSegment(sketch, "E152.2.0", {"start": v(1348.93, 173.81) * mm, "end": v(1336, 160.88) * mm});
            skLineSegment(sketch, "E152.3.0", {"start": v(1336, 258.57) * mm, "end": v(1348.93, 245.64) * mm});
            skLineSegment(sketch, "E153", {"start": v(863.58, 280.51) * mm, "end": v(863.58, 305.91) * mm, "construction": true});
            skLineSegment(sketch, "E154", {"start": v(863.58, 305.91) * mm, "end": v(812.78, 305.91) * mm});
            skLineSegment(sketch, "E155", {"start": v(812.78, 305.91) * mm, "end": v(812.78, 293.21) * mm});
            skPoint(sketch, "E155.endSnap0", {"position": v(863.58, 293.21) * mm});
            skLineSegment(sketch, "E156", {"start": v(812.78, 293.21) * mm, "end": v(850.88, 293.21) * mm});
            skLineSegment(sketch, "E157", {"start": v(850.88, 293.21) * mm, "end": v(850.88, 280.51) * mm});
            skLineSegment(sketch, "E158.MirrorCS", {"start": v(863.58, 305.91) * mm, "end": v(914.38, 305.91) * mm});
            skLineSegment(sketch, "E159.MirrorCS", {"start": v(914.38, 305.91) * mm, "end": v(914.38, 293.21) * mm});
            skLineSegment(sketch, "E160.MirrorCS", {"start": v(914.38, 293.21) * mm, "end": v(876.28, 293.21) * mm});
            skLineSegment(sketch, "E161.MirrorCS", {"start": v(876.28, 293.21) * mm, "end": v(876.28, 280.51) * mm});
            skLineSegment(sketch, "E162.1.0", {"start": v(767.4, 209.73) * mm, "end": v(767.4, 260.53) * mm});
            skLineSegment(sketch, "E162.1.1", {"start": v(767.4, 260.53) * mm, "end": v(780.1, 260.53) * mm});
            skLineSegment(sketch, "E162.1.2", {"start": v(780.1, 260.53) * mm, "end": v(780.1, 222.43) * mm});
            skPoint(sketch, "E162.1.3", {"position": v(780.1, 209.73) * mm});
            skLineSegment(sketch, "E162.1.4", {"start": v(767.4, 209.73) * mm, "end": v(767.4, 158.93) * mm});
            skLineSegment(sketch, "E162.1.5", {"start": v(767.4, 158.93) * mm, "end": v(780.1, 158.93) * mm});
            skLineSegment(sketch, "E162.1.6", {"start": v(780.1, 158.93) * mm, "end": v(780.1, 197.03) * mm});
            skLineSegment(sketch, "E162.1.7", {"start": v(780.1, 197.03) * mm, "end": v(792.8, 197.03) * mm});
            skLineSegment(sketch, "E162.1.8", {"start": v(780.1, 222.43) * mm, "end": v(792.8, 222.43) * mm});
            skLineSegment(sketch, "E162.2.0", {"start": v(863.58, 113.54) * mm, "end": v(812.78, 113.54) * mm});
            skLineSegment(sketch, "E162.2.1", {"start": v(812.78, 113.54) * mm, "end": v(812.78, 126.24) * mm});
            skLineSegment(sketch, "E162.2.2", {"start": v(812.78, 126.24) * mm, "end": v(850.88, 126.24) * mm});
            skPoint(sketch, "E162.2.3", {"position": v(863.58, 126.24) * mm});
            skLineSegment(sketch, "E162.2.4", {"start": v(863.58, 113.54) * mm, "end": v(914.38, 113.54) * mm});
            skLineSegment(sketch, "E162.2.5", {"start": v(914.38, 113.54) * mm, "end": v(914.38, 126.24) * mm});
            skLineSegment(sketch, "E162.2.6", {"start": v(914.38, 126.24) * mm, "end": v(876.28, 126.24) * mm});
            skLineSegment(sketch, "E162.2.7", {"start": v(876.28, 126.24) * mm, "end": v(876.28, 138.94) * mm});
            skLineSegment(sketch, "E162.2.8", {"start": v(850.88, 126.24) * mm, "end": v(850.88, 138.94) * mm});
            skLineSegment(sketch, "E162.3.0", {"start": v(959.77, 209.73) * mm, "end": v(959.77, 158.93) * mm});
            skLineSegment(sketch, "E162.3.1", {"start": v(959.77, 158.93) * mm, "end": v(947.07, 158.93) * mm});
            skLineSegment(sketch, "E162.3.2", {"start": v(947.07, 158.93) * mm, "end": v(947.07, 197.03) * mm});
            skPoint(sketch, "E162.3.3", {"position": v(947.07, 209.73) * mm});
            skLineSegment(sketch, "E162.3.4", {"start": v(959.77, 209.73) * mm, "end": v(959.77, 260.53) * mm});
            skLineSegment(sketch, "E162.3.5", {"start": v(959.77, 260.53) * mm, "end": v(947.07, 260.53) * mm});
            skLineSegment(sketch, "E162.3.6", {"start": v(947.07, 260.53) * mm, "end": v(947.07, 222.43) * mm});
            skLineSegment(sketch, "E162.3.7", {"start": v(947.07, 222.43) * mm, "end": v(934.37, 222.43) * mm});
            skLineSegment(sketch, "E162.3.8", {"start": v(947.07, 197.03) * mm, "end": v(934.37, 197.03) * mm});
            skLineSegment(sketch, "E163", {"start": v(1300.09, 258.57) * mm, "end": v(1300.09, 283.97) * mm, "construction": true});
            skLineSegment(sketch, "E164", {"start": v(1300.09, 283.97) * mm, "end": v(1266.43, 283.97) * mm});
            skLineSegment(sketch, "E165", {"start": v(1266.43, 283.97) * mm, "end": v(1266.43, 271.27) * mm});
            skPoint(sketch, "E165.endSnap0", {"position": v(1300.09, 271.27) * mm});
            skLineSegment(sketch, "E166", {"start": v(1266.43, 271.27) * mm, "end": v(1291.83, 271.27) * mm});
            skLineSegment(sketch, "E167", {"start": v(1291.83, 271.27) * mm, "end": v(1291.83, 258.57) * mm});
            skLineSegment(sketch, "E168.MirrorCS", {"start": v(1300.09, 283.97) * mm, "end": v(1333.74, 283.97) * mm});
            skLineSegment(sketch, "E169.MirrorCS", {"start": v(1333.74, 283.97) * mm, "end": v(1333.74, 271.27) * mm});
            skLineSegment(sketch, "E170.MirrorCS", {"start": v(1333.74, 271.27) * mm, "end": v(1308.34, 271.27) * mm});
            skLineSegment(sketch, "E171.MirrorCS", {"start": v(1308.34, 271.27) * mm, "end": v(1308.34, 258.57) * mm});
            skLineSegment(sketch, "E172.1.0", {"start": v(1225.84, 209.73) * mm, "end": v(1225.84, 243.38) * mm});
            skLineSegment(sketch, "E172.1.1", {"start": v(1225.84, 243.38) * mm, "end": v(1238.54, 243.38) * mm});
            skLineSegment(sketch, "E172.1.2", {"start": v(1238.54, 243.38) * mm, "end": v(1238.54, 217.98) * mm});
            skPoint(sketch, "E172.1.3", {"position": v(1238.54, 209.73) * mm});
            skLineSegment(sketch, "E172.1.4", {"start": v(1225.84, 209.73) * mm, "end": v(1225.84, 176.07) * mm});
            skLineSegment(sketch, "E172.1.5", {"start": v(1225.84, 176.07) * mm, "end": v(1238.54, 176.07) * mm});
            skLineSegment(sketch, "E172.1.6", {"start": v(1238.54, 176.07) * mm, "end": v(1238.54, 201.47) * mm});
            skLineSegment(sketch, "E172.1.7", {"start": v(1238.54, 217.98) * mm, "end": v(1251.24, 217.98) * mm});
            skLineSegment(sketch, "E172.1.8", {"start": v(1238.54, 201.47) * mm, "end": v(1251.24, 201.47) * mm});
            skLineSegment(sketch, "E172.2.0", {"start": v(1300.09, 135.48) * mm, "end": v(1266.43, 135.48) * mm});
            skLineSegment(sketch, "E172.2.1", {"start": v(1266.43, 135.48) * mm, "end": v(1266.43, 148.18) * mm});
            skLineSegment(sketch, "E172.2.2", {"start": v(1266.43, 148.18) * mm, "end": v(1291.83, 148.18) * mm});
            skPoint(sketch, "E172.2.3", {"position": v(1300.09, 148.18) * mm});
            skLineSegment(sketch, "E172.2.4", {"start": v(1300.09, 135.48) * mm, "end": v(1333.74, 135.48) * mm});
            skLineSegment(sketch, "E172.2.5", {"start": v(1333.74, 135.48) * mm, "end": v(1333.74, 148.18) * mm});
            skLineSegment(sketch, "E172.2.6", {"start": v(1333.74, 148.18) * mm, "end": v(1308.34, 148.18) * mm});
            skLineSegment(sketch, "E172.2.7", {"start": v(1291.83, 148.18) * mm, "end": v(1291.83, 160.88) * mm});
            skLineSegment(sketch, "E172.2.8", {"start": v(1308.34, 148.18) * mm, "end": v(1308.34, 160.88) * mm});
            skLineSegment(sketch, "E172.3.0", {"start": v(1374.33, 209.73) * mm, "end": v(1374.33, 176.07) * mm});
            skLineSegment(sketch, "E172.3.1", {"start": v(1374.33, 176.07) * mm, "end": v(1361.63, 176.07) * mm});
            skLineSegment(sketch, "E172.3.2", {"start": v(1361.63, 176.07) * mm, "end": v(1361.63, 201.47) * mm});
            skPoint(sketch, "E172.3.3", {"position": v(1361.63, 209.73) * mm});
            skLineSegment(sketch, "E172.3.4", {"start": v(1374.33, 209.73) * mm, "end": v(1374.33, 243.38) * mm});
            skLineSegment(sketch, "E172.3.5", {"start": v(1374.33, 243.38) * mm, "end": v(1361.63, 243.38) * mm});
            skLineSegment(sketch, "E172.3.6", {"start": v(1361.63, 243.38) * mm, "end": v(1361.63, 217.98) * mm});
            skLineSegment(sketch, "E172.3.7", {"start": v(1361.63, 201.47) * mm, "end": v(1348.93, 201.47) * mm});
            skLineSegment(sketch, "E172.3.8", {"start": v(1361.63, 217.98) * mm, "end": v(1348.93, 217.98) * mm});
            skLineSegment(sketch, "E173", {"start": v(906.56, 20.3) * mm, "end": v(923.35, 43.41) * mm, "construction": true});
            skLineSegment(sketch, "E174", {"start": v(923.35, 43.41) * mm, "end": v(892.53, 65.8) * mm});
            skLineSegment(sketch, "E175", {"start": v(892.53, 65.8) * mm, "end": v(885.07, 55.53) * mm});
            skLineSegment(sketch, "E176", {"start": v(885.07, 55.53) * mm, "end": v(905.62, 40.6) * mm});
            skLineSegment(sketch, "E177", {"start": v(905.62, 40.6) * mm, "end": v(896.28, 27.76) * mm});
            skLineSegment(sketch, "E178.MirrorCS", {"start": v(923.35, 43.41) * mm, "end": v(954.18, 21.02) * mm});
            skLineSegment(sketch, "E179.MirrorCS", {"start": v(954.18, 21.02) * mm, "end": v(946.71, 10.74) * mm});
            skLineSegment(sketch, "E180.MirrorCS", {"start": v(946.71, 10.74) * mm, "end": v(926.16, 25.67) * mm});
            skLineSegment(sketch, "E181.MirrorCS", {"start": v(926.16, 25.67) * mm, "end": v(916.83, 12.83) * mm});
            skLineSegment(sketch, "E182.1.0", {"start": v(780.45, 10.74) * mm, "end": v(801, 25.67) * mm});
            skLineSegment(sketch, "E182.1.1", {"start": v(801, 25.67) * mm, "end": v(810.33, 12.83) * mm});
            skLineSegment(sketch, "E182.1.2", {"start": v(803.8, 43.41) * mm, "end": v(834.63, 65.8) * mm});
            skLineSegment(sketch, "E182.1.3", {"start": v(834.63, 65.8) * mm, "end": v(842.1, 55.53) * mm});
            skLineSegment(sketch, "E182.1.4", {"start": v(842.1, 55.53) * mm, "end": v(821.54, 40.6) * mm});
            skLineSegment(sketch, "E182.1.5", {"start": v(821.54, 40.6) * mm, "end": v(830.87, 27.76) * mm});
            skPoint(sketch, "E182.1.6", {"position": v(820.6, 20.3) * mm});
            skLineSegment(sketch, "E182.1.7", {"start": v(820.6, 20.3) * mm, "end": v(803.8, 43.41) * mm, "construction": true});
            skLineSegment(sketch, "E182.1.8", {"start": v(803.8, 43.41) * mm, "end": v(772.98, 21.02) * mm});
            skLineSegment(sketch, "E182.1.9", {"start": v(772.98, 21.02) * mm, "end": v(780.45, 10.74) * mm});
            skLineSegment(sketch, "E182.2.0", {"start": v(790.71, -102.6) * mm, "end": v(782.86, -78.44) * mm});
            skLineSegment(sketch, "E182.2.1", {"start": v(782.86, -78.44) * mm, "end": v(797.96, -73.54) * mm});
            skLineSegment(sketch, "E182.2.2", {"start": v(766.86, -70.29) * mm, "end": v(755.09, -34.05) * mm});
            skLineSegment(sketch, "E182.2.3", {"start": v(755.09, -34.05) * mm, "end": v(767.17, -30.13) * mm});
            skLineSegment(sketch, "E182.2.4", {"start": v(767.17, -30.13) * mm, "end": v(775.02, -54.28) * mm});
            skLineSegment(sketch, "E182.2.5", {"start": v(775.02, -54.28) * mm, "end": v(790.11, -49.38) * mm});
            skPoint(sketch, "E182.2.6", {"position": v(794.04, -61.46) * mm});
            skLineSegment(sketch, "E182.2.7", {"start": v(794.04, -61.46) * mm, "end": v(766.86, -70.29) * mm, "construction": true});
            skLineSegment(sketch, "E182.2.8", {"start": v(766.86, -70.29) * mm, "end": v(778.63, -106.52) * mm});
            skLineSegment(sketch, "E182.2.9", {"start": v(778.63, -106.52) * mm, "end": v(790.71, -102.6) * mm});
            skLineSegment(sketch, "E182.3.0", {"start": v(901.68, -127.86) * mm, "end": v(876.28, -127.86) * mm});
            skLineSegment(sketch, "E182.3.1", {"start": v(876.28, -127.86) * mm, "end": v(876.28, -111.98) * mm});
            skLineSegment(sketch, "E182.3.2", {"start": v(863.58, -140.56) * mm, "end": v(825.48, -140.56) * mm});
            skLineSegment(sketch, "E182.3.3", {"start": v(825.48, -140.56) * mm, "end": v(825.48, -127.86) * mm});
            skLineSegment(sketch, "E182.3.4", {"start": v(825.48, -127.86) * mm, "end": v(850.88, -127.86) * mm});
            skLineSegment(sketch, "E182.3.5", {"start": v(850.88, -127.86) * mm, "end": v(850.88, -111.98) * mm});
            skPoint(sketch, "E182.3.6", {"position": v(863.58, -111.98) * mm});
            skLineSegment(sketch, "E182.3.7", {"start": v(863.58, -111.98) * mm, "end": v(863.58, -140.56) * mm, "construction": true});
            skLineSegment(sketch, "E182.3.8", {"start": v(863.58, -140.56) * mm, "end": v(901.68, -140.56) * mm});
            skLineSegment(sketch, "E182.3.9", {"start": v(901.68, -140.56) * mm, "end": v(901.68, -127.86) * mm});
            skLineSegment(sketch, "E182.4.0", {"start": v(960, -30.13) * mm, "end": v(952.14, -54.28) * mm});
            skLineSegment(sketch, "E182.4.1", {"start": v(952.14, -54.28) * mm, "end": v(937.05, -49.38) * mm});
            skLineSegment(sketch, "E182.4.2", {"start": v(960.3, -70.29) * mm, "end": v(948.52, -106.52) * mm});
            skLineSegment(sketch, "E182.4.3", {"start": v(948.52, -106.52) * mm, "end": v(936.45, -102.6) * mm});
            skLineSegment(sketch, "E182.4.4", {"start": v(936.45, -102.6) * mm, "end": v(944.3, -78.44) * mm});
            skLineSegment(sketch, "E182.4.5", {"start": v(944.3, -78.44) * mm, "end": v(929.2, -73.54) * mm});
            skPoint(sketch, "E182.4.6", {"position": v(933.12, -61.46) * mm});
            skLineSegment(sketch, "E182.4.7", {"start": v(933.12, -61.46) * mm, "end": v(960.3, -70.29) * mm, "construction": true});
            skLineSegment(sketch, "E182.4.8", {"start": v(960.3, -70.29) * mm, "end": v(972.07, -34.05) * mm});
            skLineSegment(sketch, "E182.4.9", {"start": v(972.07, -34.05) * mm, "end": v(960, -30.13) * mm});
            skLineSegment(sketch, "E183.0", {"start": v(854.44, 13.13) * mm, "end": v(872.72, 13.13) * mm});
            skLineSegment(sketch, "E184.0", {"start": v(910.2, -14.1) * mm, "end": v(915.85, -31.5) * mm});
            skLineSegment(sketch, "E185.0", {"start": v(811.3, -31.5) * mm, "end": v(816.96, -14.1) * mm});
            skLineSegment(sketch, "E186.0", {"start": v(901.54, -75.55) * mm, "end": v(886.74, -86.3) * mm});
            skLineSegment(sketch, "E187.0", {"start": v(840.42, -86.3) * mm, "end": v(825.62, -75.55) * mm});
            skLineSegment(sketch, "E188", {"start": v(872.72, 13.13) * mm, "end": v(910.2, -14.1) * mm});
            skLineSegment(sketch, "E189", {"start": v(915.85, -31.5) * mm, "end": v(901.54, -75.55) * mm});
            skLineSegment(sketch, "E190", {"start": v(886.74, -86.3) * mm, "end": v(840.42, -86.3) * mm});
            skLineSegment(sketch, "E191", {"start": v(825.62, -75.55) * mm, "end": v(811.3, -31.5) * mm});
            skLineSegment(sketch, "E192", {"start": v(816.96, -14.1) * mm, "end": v(854.44, 13.13) * mm});
            skLineSegment(sketch, "E193", {"start": v(903.77, -78.63) * mm, "end": v(901.54, -75.55) * mm, "construction": true});
            skLineSegment(sketch, "E194", {"start": v(823.38, -78.63) * mm, "end": v(825.62, -75.55) * mm, "construction": true});
            skLineSegment(sketch, "E195", {"start": v(807.69, -30.32) * mm, "end": v(811.3, -31.5) * mm, "construction": true});
            skLineSegment(sketch, "E196.0", {"start": v(1077.65, 14.28) * mm, "end": v(1096.34, 14.28) * mm});
            skLineSegment(sketch, "E197.0", {"start": v(1134.65, -13.55) * mm, "end": v(1140.42, -31.33) * mm});
            skLineSegment(sketch, "E198.0", {"start": v(1033.57, -31.33) * mm, "end": v(1039.35, -13.55) * mm});
            skLineSegment(sketch, "E199.0", {"start": v(1125.8, -76.36) * mm, "end": v(1110.67, -87.35) * mm});
            skLineSegment(sketch, "E200.0", {"start": v(1063.32, -87.35) * mm, "end": v(1048.2, -76.36) * mm});
            skLineSegment(sketch, "E201", {"start": v(1096.34, 14.28) * mm, "end": v(1134.65, -13.55) * mm});
            skLineSegment(sketch, "E202", {"start": v(1140.42, -31.33) * mm, "end": v(1125.8, -76.36) * mm});
            skLineSegment(sketch, "E203", {"start": v(1110.67, -87.35) * mm, "end": v(1063.32, -87.35) * mm});
            skLineSegment(sketch, "E204", {"start": v(1048.2, -76.36) * mm, "end": v(1033.57, -31.33) * mm});
            skLineSegment(sketch, "E205", {"start": v(1039.35, -13.55) * mm, "end": v(1077.65, 14.28) * mm});
            skLineSegment(sketch, "E206", {"start": v(1087, 14.28) * mm, "end": v(1087, -87.35) * mm, "construction": true});
            skLineSegment(sketch, "E207", {"start": v(1058.5, 0.36) * mm, "end": v(1118.23, -81.85) * mm, "construction": true});
            skLineSegment(sketch, "E208", {"start": v(1040.89, -53.84) * mm, "end": v(1137.53, -22.44) * mm, "construction": true});
            skPoint(sketch, "E209", {"position": v(1087, -38.86) * mm});
            skLineSegment(sketch, "E210", {"start": v(1063.83, 260.76) * mm, "end": v(1066.52, 258.06) * mm, "construction": true});
            skLineSegment(sketch, "E211", {"start": v(1140.03, 260.76) * mm, "end": v(1137.33, 258.06) * mm, "construction": true});
            skSolve(sketch);
        }
        {
            var Q0;
            {var subQ3=sQuery(id+"F1.wireOp",EDGE,"E0.right");Q0=makeQuery(id+"F1.imprint","IMPRINT",FACE,{"disambiguationData":[TD([[makeQuery(id+"F1.imprint","IMPRINT",EDGE,{"derivedFrom":subQ3}),1.0]])]});}
            var Q1;
            Q1=makeQuery(id+"F1.imprint","IMPRINT",FACE,{"disambiguationData":[TD([[makeQuery(id+"F1.imprint","IMPRINT",EDGE,{"derivedFrom":sQuery(id+"F1.wireOp",EDGE,"E1.top")}),1.0]])]});
            var Q2;
            Q2=makeQuery(id+"F1.imprint","IMPRINT",FACE,{"disambiguationData":[TD([[makeQuery(id+"F1.imprint","IMPRINT",EDGE,{"derivedFrom":sQuery(id+"F1.wireOp",EDGE,"E1.top")}),-1.0]])]});
            var Q3;
            {var subQ3=sQuery(id+"F1.wireOp",EDGE,"E3.bottom");Q3=makeQuery(id+"F1.imprint","IMPRINT",FACE,{"disambiguationData":[TD([[makeQuery(id+"F1.imprint","IMPRINT",EDGE,{"derivedFrom":subQ3}),-1.0]])]});}
            var Q4;
            {var subQ0=sQuery(id+"F1.wireOp",EDGE,"E2.left");Q4=makeQuery(id+"F1.imprint","IMPRINT",FACE,{"disambiguationData":[TD([[makeQuery(id+"F1.imprint","IMPRINT",EDGE,{"derivedFrom":subQ0}),-1.0]])]});}
            var Q5;
            {var subQ0=sQuery(id+"F1.wireOp",EDGE,"E2.bottom");var subQ1=sQuery(id+"F1.wireOp",EDGE,"E0.left");var subQ2=makeQuery(id+"F1.imprint","INTERSECT",VERTEX,{"derivedFrom":[subQ1,subQ0]});Q5=makeQuery(id+"F1.imprint","IMPRINT",FACE,{"disambiguationData":[TD([[makeQuery(id+"F1.imprint","IMPRINT",EDGE,{"disambiguationData":[TD([[subQ2,1.0]])],"derivedFrom":subQ1}),1.0]])]});}
            var Q6;
            Q6=makeQuery(id+"F1.imprint","IMPRINT",FACE,{"disambiguationData":[TD([[makeQuery(id+"F1.imprint","IMPRINT",EDGE,{"derivedFrom":sQuery(id+"F1.wireOp",EDGE,"E7.1")}),1.0]])]});
            var Q7;
            Q7=makeQuery(id+"F1.imprint","IMPRINT",FACE,{"disambiguationData":[TD([[makeQuery(id+"F1.imprint","IMPRINT",EDGE,{"derivedFrom":sQuery(id+"F1.wireOp",EDGE,"E7.0")}),-1.0]])]});
            var Q8;
            Q8=makeQuery(id+"F1.imprint","IMPRINT",FACE,{"disambiguationData":[TD([[makeQuery(id+"F1.imprint","IMPRINT",EDGE,{"derivedFrom":sQuery(id+"F1.wireOp",EDGE,"E7.2")}),1.0]])]});
            var Q9;
            Q9=makeQuery(id+"F1.imprint","IMPRINT",FACE,{"disambiguationData":[TD([[makeQuery(id+"F1.imprint","IMPRINT",EDGE,{"derivedFrom":sQuery(id+"F1.wireOp",EDGE,"E7.0")}),1.0]])]});
            var Q10;
            Q10=makeQuery(id+"F1.imprint","IMPRINT",FACE,{"disambiguationData":[TD([[makeQuery(id+"F1.imprint","IMPRINT",EDGE,{"derivedFrom":sQuery(id+"F1.wireOp",EDGE,"E11.0")}),1.0]])]});
            var Q11;
            {var subQ1=sQuery(id+"F1.wireOp",EDGE,"E99.1.0");Q11=makeQuery(id+"F1.imprint","IMPRINT",FACE,{"disambiguationData":[TD([[makeQuery(id+"F1.imprint","IMPRINT",EDGE,{"derivedFrom":subQ1}),1.0]])]});}
            var Q12;
            Q12=makeQuery(id+"F1.imprint","IMPRINT",FACE,{"disambiguationData":[TD([[makeQuery(id+"F1.imprint","IMPRINT",EDGE,{"derivedFrom":sQuery(id+"F1.wireOp",EDGE,"E91")}),1.0]])]});
            var Q13;
            {var subQ1=sQuery(id+"F1.wireOp",EDGE,"E99.2.0");Q13=makeQuery(id+"F1.imprint","IMPRINT",FACE,{"disambiguationData":[TD([[makeQuery(id+"F1.imprint","IMPRINT",EDGE,{"derivedFrom":subQ1}),1.0]])]});}
            var Q14;
            {var subQ6=sQuery(id+"F1.wireOp",EDGE,"E79");Q14=makeQuery(id+"F1.imprint","IMPRINT",FACE,{"disambiguationData":[TD([[makeQuery(id+"F1.imprint","IMPRINT",EDGE,{"derivedFrom":subQ6}),1.0]])]});}
            var Q15;
            {var subQ2=sQuery(id+"F1.wireOp",EDGE,"E89.1.3");Q15=makeQuery(id+"F1.imprint","IMPRINT",FACE,{"disambiguationData":[TD([[makeQuery(id+"F1.imprint","IMPRINT",EDGE,{"derivedFrom":subQ2}),1.0]])]});}
            var Q16;
            {var subQ2=sQuery(id+"F1.wireOp",EDGE,"E89.1.7");Q16=makeQuery(id+"F1.imprint","IMPRINT",FACE,{"disambiguationData":[TD([[makeQuery(id+"F1.imprint","IMPRINT",EDGE,{"derivedFrom":subQ2}),-1.0]])]});}
            var Q17;
            {var subQ0=sQuery(id+"F1.wireOp",EDGE,"E89.1.0");Q17=makeQuery(id+"F1.imprint","IMPRINT",FACE,{"disambiguationData":[TD([[makeQuery(id+"F1.imprint","IMPRINT",EDGE,{"derivedFrom":subQ0}),1.0]])]});}
            var Q18;
            {var subQ0=sQuery(id+"F1.wireOp",EDGE,"E83");Q18=makeQuery(id+"F1.imprint","IMPRINT",FACE,{"disambiguationData":[TD([[makeQuery(id+"F1.imprint","IMPRINT",EDGE,{"derivedFrom":subQ0}),1.0]])]});}
            var Q19;
            {var subQ0=sQuery(id+"F1.wireOp",EDGE,"E84.MirrorCS");Q19=makeQuery(id+"F1.imprint","IMPRINT",FACE,{"disambiguationData":[TD([[makeQuery(id+"F1.imprint","IMPRINT",EDGE,{"derivedFrom":subQ0}),-1.0]])]});}
            var Q20;
            {var subQ0=sQuery(id+"F1.wireOp",EDGE,"E89.2.0");Q20=makeQuery(id+"F1.imprint","IMPRINT",FACE,{"disambiguationData":[TD([[makeQuery(id+"F1.imprint","IMPRINT",EDGE,{"derivedFrom":subQ0}),1.0]])]});}
            var Q21;
            {var subQ2=sQuery(id+"F1.wireOp",EDGE,"E89.2.3");Q21=makeQuery(id+"F1.imprint","IMPRINT",FACE,{"disambiguationData":[TD([[makeQuery(id+"F1.imprint","IMPRINT",EDGE,{"derivedFrom":subQ2}),1.0]])]});}
            var Q22;
            {var subQ2=sQuery(id+"F1.wireOp",EDGE,"E89.2.7");Q22=makeQuery(id+"F1.imprint","IMPRINT",FACE,{"disambiguationData":[TD([[makeQuery(id+"F1.imprint","IMPRINT",EDGE,{"derivedFrom":subQ2}),-1.0]])]});}
            var Q23;
            {var subQ3=sQuery(id+"F1.wireOp",EDGE,"E103");Q23=makeQuery(id+"F1.imprint","IMPRINT",FACE,{"disambiguationData":[TD([[makeQuery(id+"F1.imprint","IMPRINT",EDGE,{"derivedFrom":subQ3}),1.0]])]});}
            var Q24;
            {var subQ6=sQuery(id+"F1.wireOp",EDGE,"E119");Q24=makeQuery(id+"F1.imprint","IMPRINT",FACE,{"disambiguationData":[TD([[makeQuery(id+"F1.imprint","IMPRINT",EDGE,{"derivedFrom":subQ6}),-1.0]])]});}
            var Q25;
            Q25=makeQuery(id+"F1.imprint","IMPRINT",FACE,{"disambiguationData":[TD([[makeQuery(id+"F1.imprint","IMPRINT",EDGE,{"derivedFrom":sQuery(id+"F1.wireOp",EDGE,"E154")}),1.0]])]});
            var Q26;
            Q26=makeQuery(id+"F1.imprint","IMPRINT",FACE,{"disambiguationData":[TD([[makeQuery(id+"F1.imprint","IMPRINT",EDGE,{"derivedFrom":sQuery(id+"F1.wireOp",EDGE,"E162.1.0")}),-1.0]])]});
            var Q27;
            Q27=makeQuery(id+"F1.imprint","IMPRINT",FACE,{"disambiguationData":[TD([[makeQuery(id+"F1.imprint","IMPRINT",EDGE,{"derivedFrom":sQuery(id+"F1.wireOp",EDGE,"E162.3.0")}),-1.0]])]});
            var Q28;
            Q28=makeQuery(id+"F1.imprint","IMPRINT",FACE,{"disambiguationData":[TD([[makeQuery(id+"F1.imprint","IMPRINT",EDGE,{"derivedFrom":sQuery(id+"F1.wireOp",EDGE,"E162.2.0")}),-1.0]])]});
            var Q29;
            Q29=makeQuery(id+"F1.imprint","IMPRINT",FACE,{"disambiguationData":[TD([[makeQuery(id+"F1.imprint","IMPRINT",EDGE,{"derivedFrom":sQuery(id+"F1.wireOp",EDGE,"E182.3.0")}),1.0]])]});
            var Q30;
            Q30=makeQuery(id+"F1.imprint","IMPRINT",FACE,{"disambiguationData":[TD([[makeQuery(id+"F1.imprint","IMPRINT",EDGE,{"derivedFrom":sQuery(id+"F1.wireOp",EDGE,"E182.2.0")}),1.0]])]});
            var Q31;
            Q31=makeQuery(id+"F1.imprint","IMPRINT",FACE,{"disambiguationData":[TD([[makeQuery(id+"F1.imprint","IMPRINT",EDGE,{"derivedFrom":sQuery(id+"F1.wireOp",EDGE,"E182.1.0")}),1.0]])]});
            var Q32;
            Q32=makeQuery(id+"F1.imprint","IMPRINT",FACE,{"disambiguationData":[TD([[makeQuery(id+"F1.imprint","IMPRINT",EDGE,{"derivedFrom":sQuery(id+"F1.wireOp",EDGE,"E174")}),1.0]])]});
            var Q33;
            Q33=makeQuery(id+"F1.imprint","IMPRINT",FACE,{"disambiguationData":[TD([[makeQuery(id+"F1.imprint","IMPRINT",EDGE,{"derivedFrom":sQuery(id+"F1.wireOp",EDGE,"E182.4.0")}),1.0]])]});
            var Q34;
            {var subQ4=sQuery(id+"F1.wireOp",EDGE,"E151");Q34=makeQuery(id+"F1.imprint","IMPRINT",FACE,{"disambiguationData":[TD([[makeQuery(id+"F1.imprint","IMPRINT",EDGE,{"derivedFrom":subQ4}),-1.0]])]});}
            var Q35;
            Q35=makeQuery(id+"F1.imprint","IMPRINT",FACE,{"disambiguationData":[TD([[makeQuery(id+"F1.imprint","IMPRINT",EDGE,{"derivedFrom":sQuery(id+"F1.wireOp",EDGE,"E196.0")}),-1.0]])]});
            var Q36;
            Q36=makeQuery(id+"F1.imprint","IMPRINT",FACE,{"disambiguationData":[TD([[makeQuery(id+"F1.imprint","IMPRINT",EDGE,{"derivedFrom":sQuery(id+"F1.wireOp",EDGE,"E164")}),1.0]])]});
            var Q37;
            Q37=makeQuery(id+"F1.imprint","IMPRINT",FACE,{"disambiguationData":[TD([[makeQuery(id+"F1.imprint","IMPRINT",EDGE,{"derivedFrom":sQuery(id+"F1.wireOp",EDGE,"E172.1.0")}),-1.0]])]});
            var Q38;
            Q38=makeQuery(id+"F1.imprint","IMPRINT",FACE,{"disambiguationData":[TD([[makeQuery(id+"F1.imprint","IMPRINT",EDGE,{"derivedFrom":sQuery(id+"F1.wireOp",EDGE,"E172.2.0")}),-1.0]])]});
            var Q39;
            Q39=makeQuery(id+"F1.imprint","IMPRINT",FACE,{"disambiguationData":[TD([[makeQuery(id+"F1.imprint","IMPRINT",EDGE,{"derivedFrom":sQuery(id+"F1.wireOp",EDGE,"E172.3.0")}),-1.0]])]});
            extrude(context, id + "F2", {"entities" : qUnion([Q0, Q1, Q2, Q3, Q4, Q5, Q6, Q7, Q8, Q9, Q10, Q11, Q12, Q13, Q14, Q15, Q16, Q17, Q18, Q19, Q20, Q21, Q22, Q23, Q24, Q25, Q26, Q27, Q28, Q29, Q30, Q31, Q32, Q33, Q34, Q35, Q36, Q37, Q38, Q39]), "depth" : (getVariable(context, 'ply34')) * mm});
        }
    });
